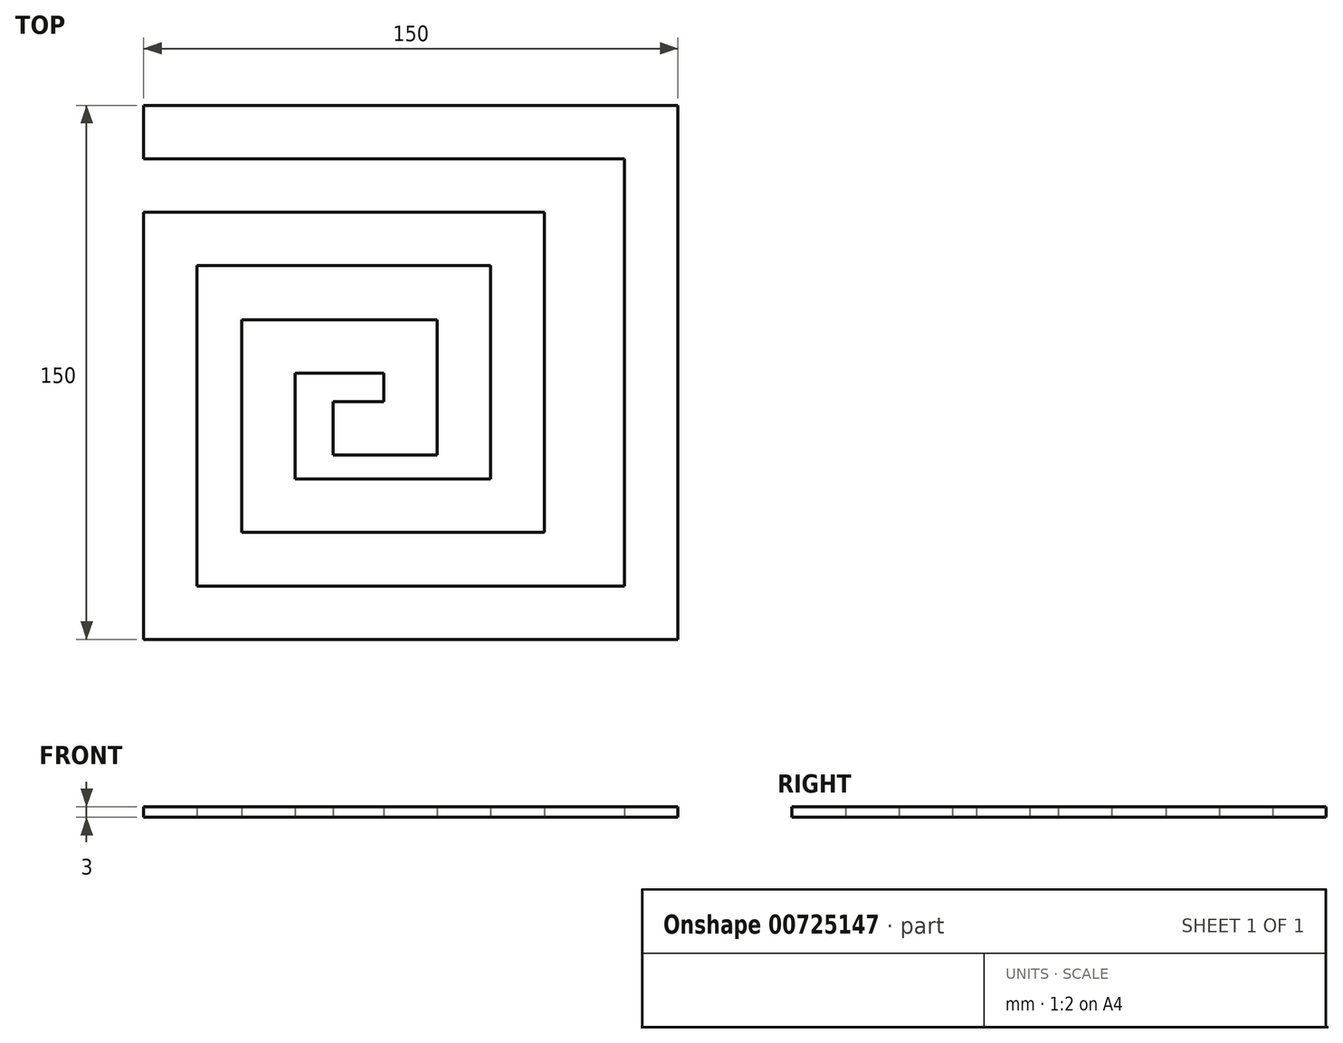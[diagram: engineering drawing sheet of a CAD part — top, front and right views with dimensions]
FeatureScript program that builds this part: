
annotation { "Feature Type Name" : "Feature", "Feature Type Description" : "" }
export const myFeature = defineFeature(function(context is Context, id is Id, definition is map)
    precondition{}
    {
        {
            var Q0;
            Q0=qCreatedBy(makeId("Top.planeOp"),FACE);
            var sketch = newSketch(context, id + "F0", { "sketchPlane" : qUnion([Q0])});
            skLineSegment(sketch, "E0.bottom", {"start": v(-75, 75) * mm, "end": v(75, 75) * mm, "construction": true});
            skLineSegment(sketch, "E0.top", {"start": v(-75, -75) * mm, "end": v(75, -75) * mm, "construction": true});
            skLineSegment(sketch, "E0.left", {"start": v(-75, 75) * mm, "end": v(-75, -75) * mm, "construction": true});
            skLineSegment(sketch, "E0.right", {"start": v(75, 75) * mm, "end": v(75, -75) * mm, "construction": true});
            skLineSegment(sketch, "E1", {"start": v(-75, 75) * mm, "end": v(75, 75) * mm});
            skLineSegment(sketch, "E2", {"start": v(75, 75) * mm, "end": v(75, -75) * mm});
            skLineSegment(sketch, "E3", {"start": v(75, -75) * mm, "end": v(-75, -75) * mm});
            skLineSegment(sketch, "E4", {"start": v(-75, -75) * mm, "end": v(-75, 45) * mm});
            skLineSegment(sketch, "E5", {"start": v(-75, 45) * mm, "end": v(37.43, 45) * mm});
            skLineSegment(sketch, "E6", {"start": v(37.43, 45) * mm, "end": v(37.43, -45) * mm});
            skLineSegment(sketch, "E7", {"start": v(37.43, -45) * mm, "end": v(-47.52, -45) * mm});
            skLineSegment(sketch, "E8", {"start": v(-47.52, -45) * mm, "end": v(-47.52, 14.8) * mm});
            skLineSegment(sketch, "E9", {"start": v(-47.52, 14.8) * mm, "end": v(7.43, 14.8) * mm});
            skLineSegment(sketch, "E10", {"start": v(7.43, 14.8) * mm, "end": v(7.43, -23.2) * mm});
            skLineSegment(sketch, "E11", {"start": v(7.43, -23.2) * mm, "end": v(-21.77, -23.2) * mm});
            skLineSegment(sketch, "E12", {"start": v(-21.77, -23.2) * mm, "end": v(-21.77, -8.2) * mm});
            skLineSegment(sketch, "E13", {"start": v(-21.77, -8.2) * mm, "end": v(-7.57, -8.2) * mm});
            skLineSegment(sketch, "E14", {"start": v(-7.57, -8.2) * mm, "end": v(-7.57, -0.2) * mm});
            skLineSegment(sketch, "E15", {"start": v(-7.57, -0.2) * mm, "end": v(-32.52, -0.2) * mm});
            skLineSegment(sketch, "E16", {"start": v(-32.52, -0.2) * mm, "end": v(-32.52, -30) * mm});
            skLineSegment(sketch, "E17", {"start": v(-32.52, -30) * mm, "end": v(22.43, -30) * mm});
            skLineSegment(sketch, "E18", {"start": v(22.43, -30) * mm, "end": v(22.43, 30) * mm});
            skLineSegment(sketch, "E19", {"start": v(22.43, 30) * mm, "end": v(-60, 30) * mm});
            skLineSegment(sketch, "E20", {"start": v(-60, 30) * mm, "end": v(-60, -60) * mm});
            skLineSegment(sketch, "E21", {"start": v(-60, -60) * mm, "end": v(60, -60) * mm});
            skLineSegment(sketch, "E22", {"start": v(60, -60) * mm, "end": v(60, 60) * mm});
            skLineSegment(sketch, "E23", {"start": v(60, 60) * mm, "end": v(-75, 60) * mm});
            skLineSegment(sketch, "E24", {"start": v(-75, 60) * mm, "end": v(-75, 75) * mm});
            skSolve(sketch);
        }
        {
            var Q0;
            Q0 = qSketchRegion(id + "F0", true);
            extrude(context, id + "F1", {"entities" : qUnion([Q0]), "depth" : 3 * mm, "offsetDistance" : 25 * mm});
        }
    });
